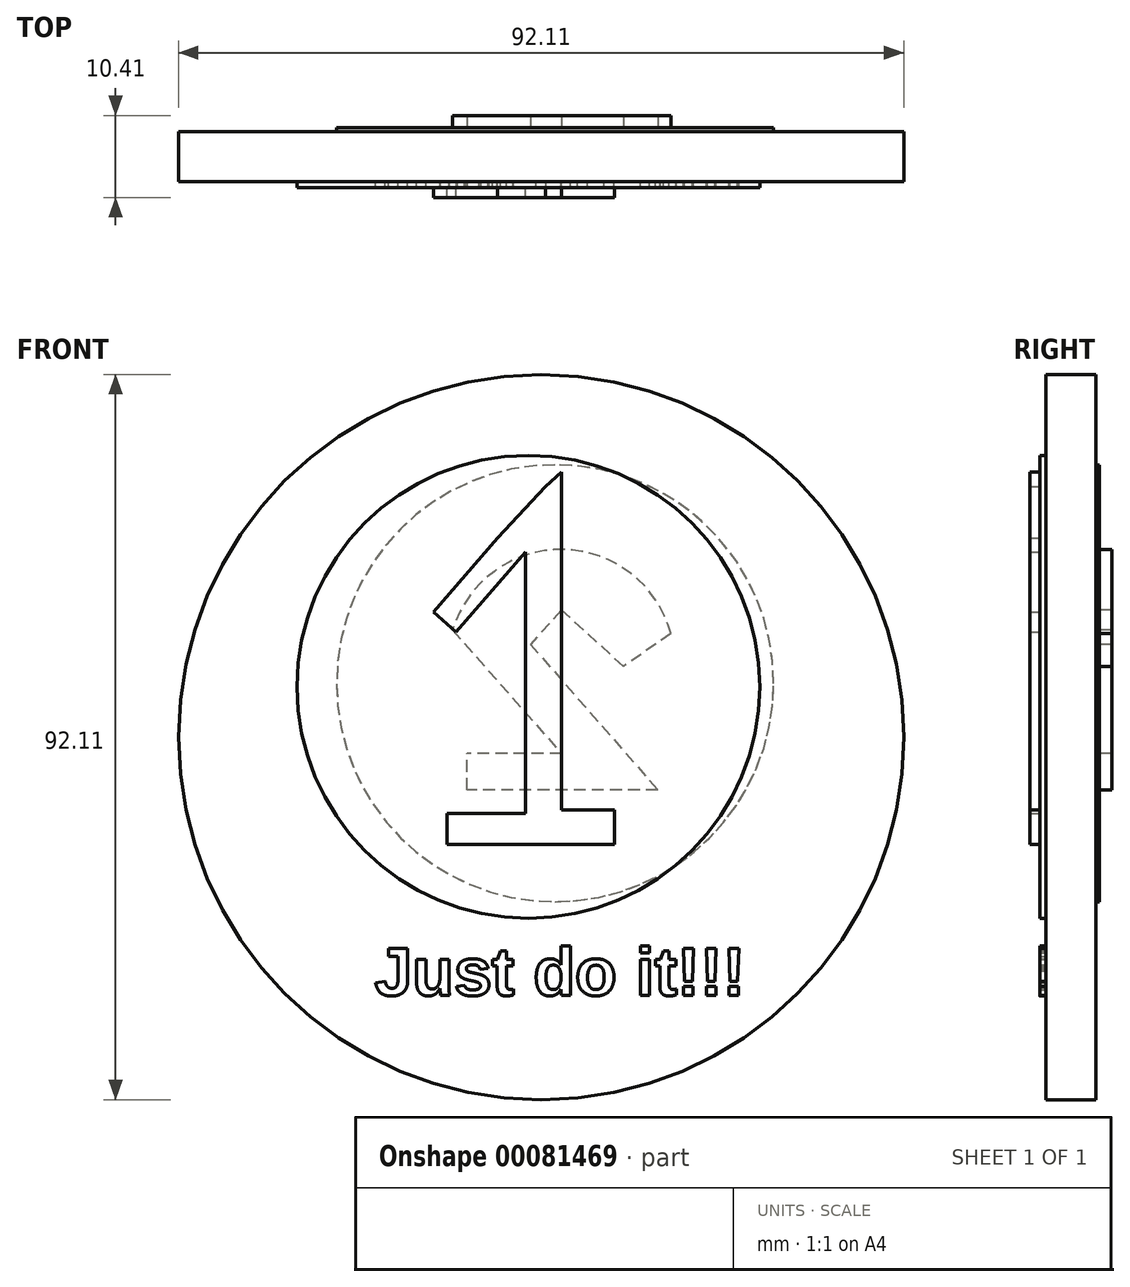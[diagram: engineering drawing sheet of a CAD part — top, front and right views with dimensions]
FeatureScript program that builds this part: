
annotation { "Feature Type Name" : "Feature", "Feature Type Description" : "" }
export const myFeature = defineFeature(function(context is Context, id is Id, definition is map)
    precondition{}
    {
        {
            var Q0;
            Q0=qCreatedBy(makeId("Front.planeOp"),FACE);
            var sketch = newSketch(context, id + "F0", { "sketchPlane" : qUnion([Q0])});
            skCircle(sketch, "E0", {"center": v(-2.6, 15.84) * mm, "radius": 46.05 * mm});
            skPoint(sketch, "E0.first.point", {"position": v(-48.66, 15.6) * mm});
            skPoint(sketch, "E0.second.point", {"position": v(-44.59, 34.76) * mm});
            skPoint(sketch, "E0.third.point", {"position": v(1.45, -30.04) * mm});
            skSolve(sketch);
        }
        {
            var Q0;
            Q0=makeQuery(id+"F0.imprint","IMPRINT",FACE,{"disambiguationData":[TD([[makeQuery(id+"F0.imprint","IMPRINT",EDGE,{"derivedFrom":sQuery(id+"F0.wireOp",EDGE,"E0")}),1.0]])]});
            extrude(context, id + "F1", {"entities" : qUnion([Q0]), "depth" : 6.35 * mm});
        }
        {
            var Q0;
            Q0=makeQuery(id+"F1.opExtrude","CAP_FACE",FACE,{"disambiguationData":[OSD([sQuery(id+"F0.wireOp",EDGE,"E0")])],"isStart":false});
            var sketch = newSketch(context, id + "F2", { "sketchPlane" : qUnion([Q0])});
            skLineSegment(sketch, "E1", {"start": v(-4.62, 39.37) * mm, "end": v(-13.4, 29.21) * mm});
            skLineSegment(sketch, "E2", {"start": v(-4.62, 39.37) * mm, "end": v(-4.62, 7.5) * mm});
            skLineSegment(sketch, "E3", {"start": v(-13.4, 29.21) * mm, "end": v(-16.28, 31.7) * mm});
            skLineSegment(sketch, "E4", {"start": v(-16.28, 31.7) * mm, "end": v(-8.14, 41.13) * mm});
            skLineSegment(sketch, "E5", {"start": v(-8.14, 41.13) * mm, "end": v(-2.08, 47.68) * mm});
            skLineSegment(sketch, "E6", {"start": v(-2.08, 47.68) * mm, "end": v(0, 49.53) * mm});
            skLineSegment(sketch, "E7", {"start": v(0, 49.53) * mm, "end": v(0, 6.58) * mm});
            skLineSegment(sketch, "E8", {"start": v(0, 6.58) * mm, "end": v(6.7, 6.58) * mm});
            skLineSegment(sketch, "E9", {"start": v(6.7, 6.58) * mm, "end": v(6.7, 2.2) * mm});
            skLineSegment(sketch, "E10", {"start": v(6.7, 2.2) * mm, "end": v(-14.55, 2.2) * mm});
            skLineSegment(sketch, "E11", {"start": v(-14.55, 2.2) * mm, "end": v(-14.55, 6.12) * mm});
            skLineSegment(sketch, "E12", {"start": v(-14.55, 6.12) * mm, "end": v(-4.62, 6.12) * mm});
            skLineSegment(sketch, "E13", {"start": v(-4.62, 6.12) * mm, "end": v(-4.62, 7.5) * mm});
            skCircle(sketch, "E14", {"center": v(-4.23, 22.23) * mm, "radius": 29.4 * mm});
            skPoint(sketch, "E14.first.point", {"position": v(-18.93, 47.68) * mm});
            skPoint(sketch, "E14.second.point", {"position": v(12.47, -1.96) * mm});
            skPoint(sketch, "E14.third.point", {"position": v(24.01, 30.36) * mm});
            skText(sketch, "E15", { "text": "Just do it!!!", "fontName": "Arimo-Bold.ttf"});
            const initialGuessF2  = {"E15": [-0.02378, -0.01697, 1, 0, 0.00623]};
            skSetInitialGuess(sketch, initialGuessF2);
            skSolve(sketch);
        }
        {
            var Q0;
            Q0 = qSketchRegion(id + "F2", true);
            extrude(context, id + "F3", {"entities" : qUnion([Q0]), "operationType" : NewBodyOperationType.ADD, "depth" : 0.76 * mm});
        }
        {
            var Q0;
            Q0=makeQuery(id+"F3.boolean.opBoolean","SPLIT",FACE,{"disambiguationData":[TD([makeQuery(id+"F3.opExtrude","SWEPT_FACE",FACE,{"disambiguationData":[OSD([sQuery(id+"F2.wireOp",EDGE,"E1")])]})])],"derivedFrom":makeQuery(id+"F1.opExtrude","CAP_FACE",FACE,{"disambiguationData":[OSD([sQuery(id+"F0.wireOp",EDGE,"E0")])],"isStart":false})});
            extrude(context, id + "F4", {"entities" : qUnion([Q0]), "operationType" : NewBodyOperationType.ADD, "depth" : 2.03 * mm});
        }
        {
            var Q0;
            Q0=makeQuery(id+"F1.opExtrude","CAP_FACE",FACE,{"disambiguationData":[OSD([sQuery(id+"F0.wireOp",EDGE,"E0")])],"isStart":true});
            var sketch = newSketch(context, id + "F5", { "sketchPlane" : qUnion([Q0])});
            skArc(sketch, "E16", {"start": v(13.85, 29.44) * mm, "mid": v(-0.17, 39.67) * mm, "end": v(-13.85, 28.98) * mm});
            skLineSegment(sketch, "E17", {"start": v(13.85, 29.44) * mm, "end": v(0, 13.74) * mm});
            skLineSegment(sketch, "E18", {"start": v(-13.85, 28.98) * mm, "end": v(-7.85, 24.82) * mm});
            skLineSegment(sketch, "E19", {"start": v(-7.85, 24.82) * mm, "end": v(0, 31.98) * mm});
            skLineSegment(sketch, "E20", {"start": v(0, 31.98) * mm, "end": v(3.97, 27.63) * mm});
            skLineSegment(sketch, "E21", {"start": v(3.97, 27.63) * mm, "end": v(-12.24, 9.12) * mm});
            skLineSegment(sketch, "E22", {"start": v(-12.24, 9.12) * mm, "end": v(12, 9.12) * mm});
            skLineSegment(sketch, "E23", {"start": v(12, 9.12) * mm, "end": v(12, 13.74) * mm});
            skLineSegment(sketch, "E24", {"start": v(0, 13.74) * mm, "end": v(12, 13.74) * mm});
            skCircle(sketch, "E25", {"center": v(0.83, 22.68) * mm, "radius": 27.75 * mm});
            skPoint(sketch, "E25.first.point", {"position": v(-21.07, 39.72) * mm});
            skPoint(sketch, "E25.second.point", {"position": v(20.89, 3.5) * mm});
            skPoint(sketch, "E25.third.point", {"position": v(-15.17, 0) * mm});
            skText(sketch, "E26", { "text": "Let your dreams be dreams...", "fontName": "RobotoSlab-Regular.ttf"});
            const initialGuessF5  = {"E26": [-0.03182, -0.01277, 1, 0, 0.00762]};
            skSetInitialGuess(sketch, initialGuessF5);
            skSolve(sketch);
        }
        {
            var Q0;
            Q0=makeQuery(id+"F5.imprint","IMPRINT",FACE,{"disambiguationData":[TD([[makeQuery(id+"F5.imprint","IMPRINT",EDGE,{"derivedFrom":sQuery(id+"F5.wireOp",EDGE,"E16")}),1.0]])]});
            extrude(context, id + "F6", {"entities" : qUnion([Q0]), "operationType" : NewBodyOperationType.ADD, "depth" : 2.03 * mm});
        }
        {
            var Q0;
            Q0=makeQuery(id+"F5.imprint","IMPRINT",FACE,{"disambiguationData":[TD([[makeQuery(id+"F5.imprint","IMPRINT",EDGE,{"derivedFrom":sQuery(id+"F5.wireOp",EDGE,"E16")}),-1.0]])]});
            extrude(context, id + "F7", {"entities" : qUnion([Q0]), "operationType" : NewBodyOperationType.ADD, "depth" : 0.5 * mm});
        }
    });
